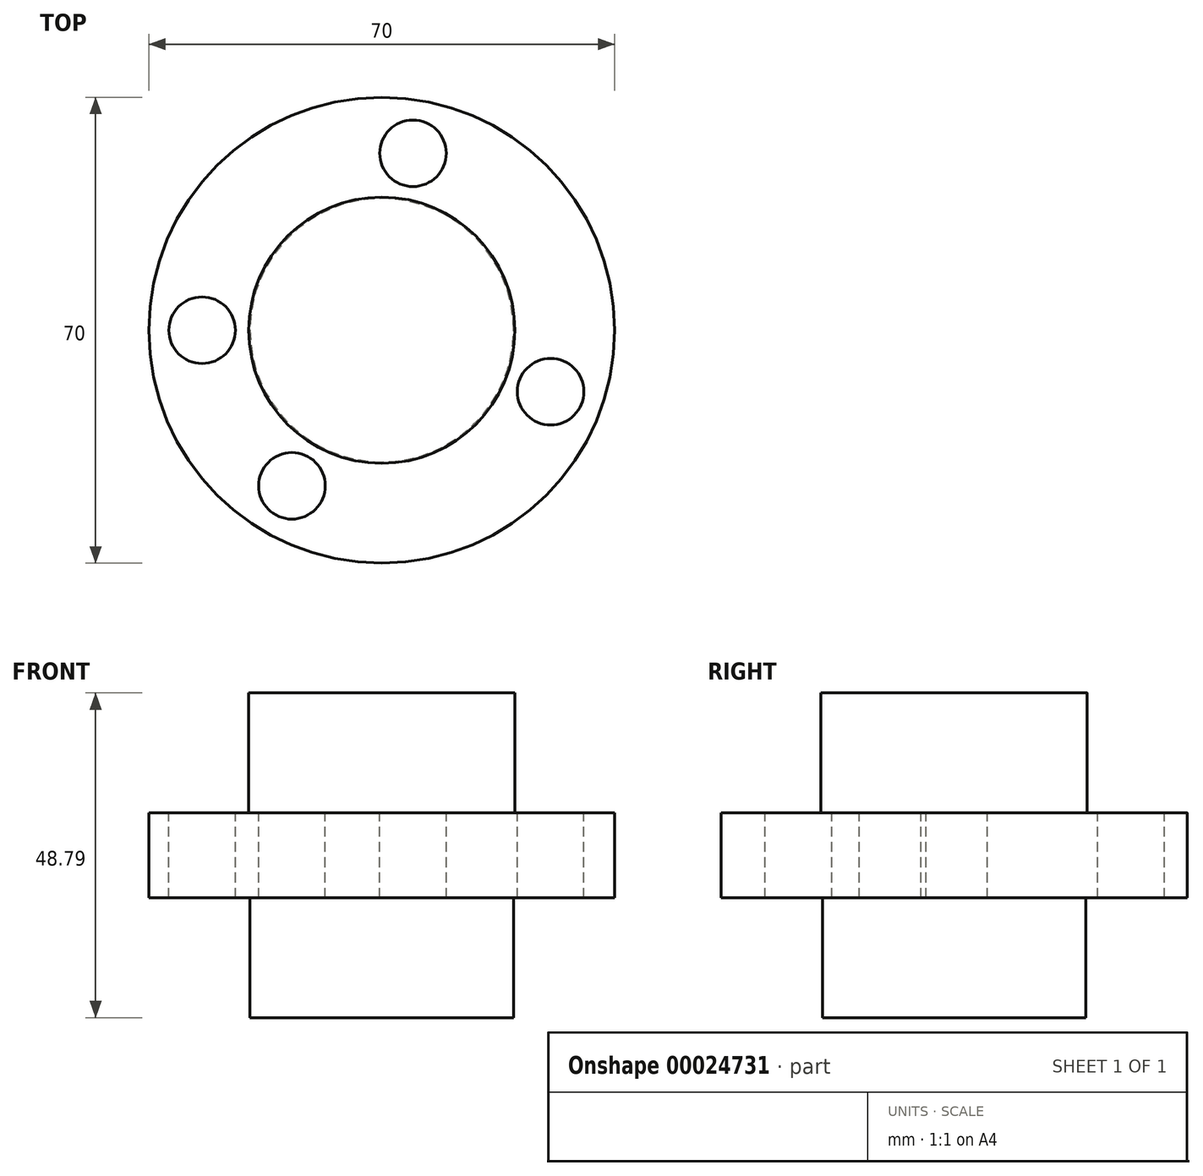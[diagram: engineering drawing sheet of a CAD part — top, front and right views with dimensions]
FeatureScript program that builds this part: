
annotation { "Feature Type Name" : "Feature", "Feature Type Description" : "" }
export const myFeature = defineFeature(function(context is Context, id is Id, definition is map)
    precondition{}
    {
        {
            var Q0;
            Q0=qCreatedBy(makeId("Front.planeOp"),FACE);
            var sketch = newSketch(context, id + "F0", { "sketchPlane" : qUnion([Q0])});
            skLineSegment(sketch, "E0", {"start": v(0, 48.79) * mm, "end": v(20, 48.79) * mm});
            skLineSegment(sketch, "E1", {"start": v(20, 48.79) * mm, "end": v(20, 30.79) * mm});
            skLineSegment(sketch, "E2", {"start": v(20, 30.79) * mm, "end": v(35, 30.79) * mm});
            skLineSegment(sketch, "E3", {"start": v(35, 30.79) * mm, "end": v(35, 18) * mm});
            skLineSegment(sketch, "E4", {"start": v(35, 18) * mm, "end": v(19.8, 18) * mm});
            skLineSegment(sketch, "E5", {"start": v(19.8, 18) * mm, "end": v(19.8, 0) * mm});
            skLineSegment(sketch, "E6", {"start": v(19.8, 0) * mm, "end": v(0, 0) * mm});
            skLineSegment(sketch, "E7", {"start": v(0, 0) * mm, "end": v(0, 48.79) * mm});
            skSolve(sketch);
        }
        {
            var Q0;
            Q0=makeQuery(id+"F0.imprint","IMPRINT",FACE,{"disambiguationData":[TD([[makeQuery(id+"F0.imprint","IMPRINT",EDGE,{"derivedFrom":sQuery(id+"F0.wireOp",EDGE,"E0")}),-1.0]])]});
            var Q1;
            Q1=sQuery(id+"F0.wireOp",EDGE,"E7");
            revolve(context, id + "F1", {"entities" : qUnion([Q0]), "axis" : qUnion([Q1]), "revolveType" : RevolveType.FULL});
        }
        {
            var Q0;
            Q0=makeQuery(id+"F1.opRevolve","SWEPT_FACE",FACE,{"disambiguationData":[OSD([sQuery(id+"F0.wireOp",EDGE,"E2")])]});
            var sketch = newSketch(context, id + "F2", { "sketchPlane" : qUnion([Q0])});
            skPoint(sketch, "E8", {"position": v(-27, 0) * mm});
            skSolve(sketch);
        }
        {
            var Q0;
            Q0=sQuery(id+"F2.wireOp",VERTEX,"E8");
            var Q1;
            Q1=makeQuery(id+"F1.opRevolve","SWEPT_BODY",BODY,{"disambiguationData":[OSD([sQuery(id+"F0.wireOp",EDGE,"E0"),sQuery(id+"F0.wireOp",EDGE,"E1"),sQuery(id+"F0.wireOp",EDGE,"E2"),sQuery(id+"F0.wireOp",EDGE,"E3"),sQuery(id+"F0.wireOp",EDGE,"E4"),sQuery(id+"F0.wireOp",EDGE,"E5"),sQuery(id+"F0.wireOp",EDGE,"E6"),sQuery(id+"F0.wireOp",EDGE,"E7")])]});
            hole(context, id + "F3", {"style" : HoleStyle.SIMPLE, "holeDiameter" : 10 * mm, "endStyle" : HoleEndStyle.BLIND, "holeDepth" : 20 * mm, "locations" : qUnion([Q0]), "scope" : qUnion([Q1])});
        }
        {
            var Q0;
            Q0=makeQuery(id+"F1.opRevolve","SWEPT_BODY",BODY,{"disambiguationData":[OSD([sQuery(id+"F0.wireOp",EDGE,"E0"),sQuery(id+"F0.wireOp",EDGE,"E1"),sQuery(id+"F0.wireOp",EDGE,"E2"),sQuery(id+"F0.wireOp",EDGE,"E3"),sQuery(id+"F0.wireOp",EDGE,"E4"),sQuery(id+"F0.wireOp",EDGE,"E5"),sQuery(id+"F0.wireOp",EDGE,"E6"),sQuery(id+"F0.wireOp",EDGE,"E7")])]});
            var Q1;
            Q1=makeQuery(id+"F1.opRevolve","SWEPT_EDGE",EDGE,{"disambiguationData":[OSD([sQuery(id+"F0.wireOp",EDGE,"E0"),sQuery(id+"F0.wireOp",EDGE,"E1")])]});
            circularPattern(context, id + "F4", {"entities" : qUnion([Q0]), "axis" : qUnion([Q1]), "angle" : 300 * degree, "instanceCount" : 4, "equalSpace" : true});
        }
    });
